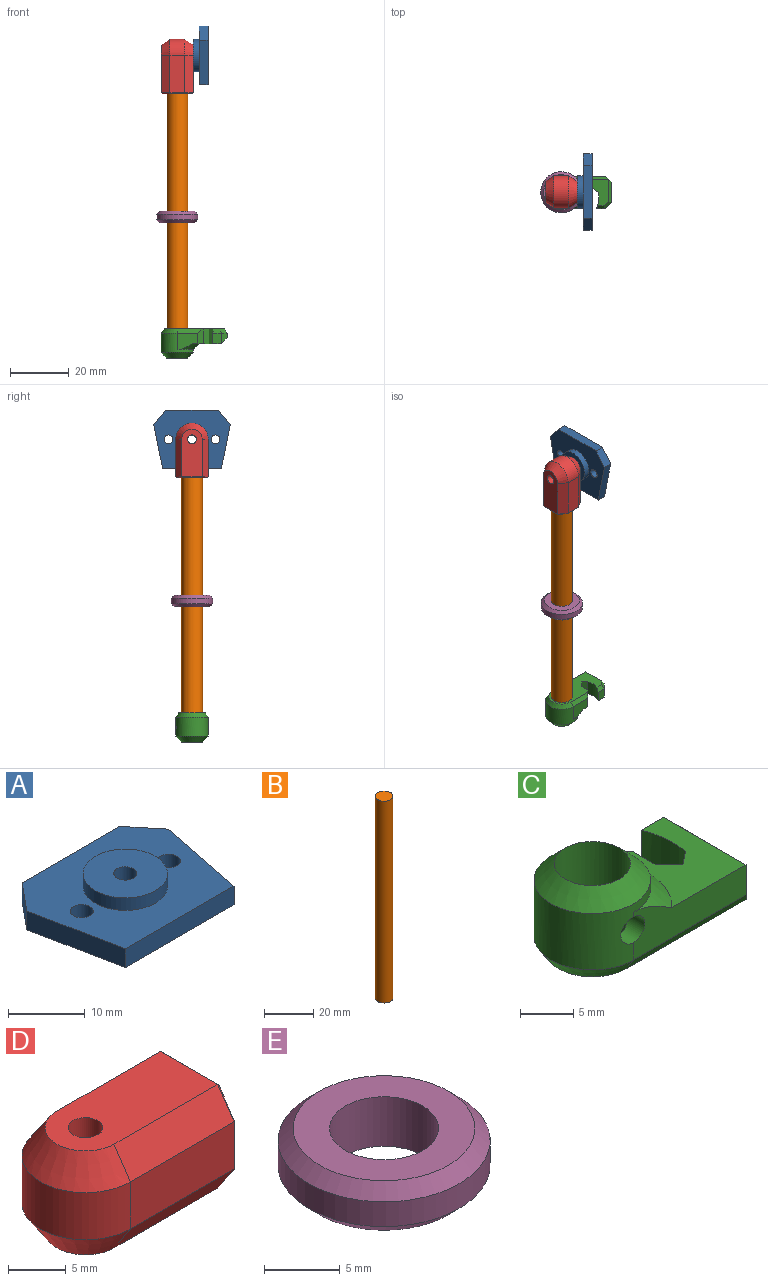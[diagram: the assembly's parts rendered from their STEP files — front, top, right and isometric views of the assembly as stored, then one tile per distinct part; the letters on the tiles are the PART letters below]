
ASSEMBLY  parts=5 mates=4
PART A: 13 faces, bbox 26x20x5 mm
  f0: plane 18x3mm, normal (0,1,0), area 54mm2, adj f7,f8,f9,f10
  f1: plane 15.1x3.02mm, normal (-0.98,-0.2,0), area 46.2mm2, adj f2,f7,f8,f10
  f2: plane 20x3mm, normal (0,-1,0), area 60mm2, adj f1,f3,f7,f8
  f3: plane 15.1x3.02mm, normal (0.98,-0.2,0), area 46.2mm2, adj f2,f7,f8,f9
  f4: cylinder r=1.5mm len=3mm, axis (0,0,1), area 28.3mm2, adj f7,f8
  f5: cylinder r=1.5mm len=3mm, axis (0,0,1), area 28.3mm2, adj f7,f8
  f6: cylinder r=1.5mm len=5mm, axis (0,0,1), area 47.1mm2, adj f7,f12
  f7: plane 26.04x20mm, normal (0,0,-1), area 434.3mm2, adj f0,f1,f2,f3,f4,f5,f6,f9
  f8: plane 26.04x20mm, normal (0,0,1), area 346.3mm2, adj f0,f1,f2,f3,f4,f5,f9,f10
  f9: plane 4.9x4.02mm, normal (0.77,0.63,0), area 19mm2, adj f0,f3,f7,f8
  f10: plane 4.9x4.02mm, normal (-0.77,0.63,0), area 19mm2, adj f0,f1,f7,f8
  f11: cylinder r=5.5mm len=11mm, axis (0,0,-1), area 69.1mm2, adj f8,f12
  f12: plane 11x11mm, normal (0,0,1), area 88mm2, adj f6,f11
PART B: 3 faces, bbox 7.2x7.2x100 mm
  f0: cylinder r=3.6mm len=100mm, axis (0,0,-1), area 2261.9mm2, adj f1,f2
  f1: plane 7.2x7.2mm, normal (0,0,1), area 40.7mm2, adj f0
  f2: plane 7.2x7.2mm, normal (0,0,-1), area 40.7mm2, adj f0
PART C: 25 faces, bbox 22.5x15x9.9 mm
  f0: plane 5x3mm, normal (1,0,0), area 15mm2, adj f8,f9,f10,f12
  f1: plane 7x5.5mm, normal (0,1,0), area 31.1mm2, adj f2,f9,f12,f16,f21
  f2: cylinder r=5.5mm len=11mm, axis (0,0,1), area 126mm2, adj f1,f3,f16,f17,f18,f20
  f3: plane 15x5.5mm, normal (0,-1,0), area 55.6mm2, adj f2,f9,f13,f16,f18,f19
  f4: plane 7x1.5mm, normal (1,0,0), area 10.5mm2, adj f13,f14,f15,f22
  f5: plane 3.5x3mm, normal (0,1,0), area 10.5mm2, adj f6,f9,f15,f24
  f6: cylinder r=9mm len=5.43mm, axis (0,0,1), area 26.9mm2, adj f5,f8,f9,f11,f24
  f7: cylinder r=3.6mm len=9.9mm, axis (0,0,1), area 216.7mm2, adj f8,f17,f18
  f8: plane 20.5x9mm, normal (0,0,-1), area 115.6mm2, adj f0,f6,f7,f10,f11,f12,f19,f20
  f9: plane 11x9.9mm, normal (0,0,1), area 67.5mm2, adj f0,f1,f3,f5,f6,f10,f11,f12
  f10: plane 5x1.8mm, normal (0.71,0.71,0), area 12.7mm2, adj f0,f8,f9,f11
  f11: plane 5x1.7mm, normal (-0.63,0.78,0), area 10.9mm2, adj f6,f8,f9,f10
  f12: plane 5x2mm, normal (0.71,0.71,0), area 13.1mm2, adj f0,f1,f8,f9,f21
  f13: plane 5x2mm, normal (0.71,-0.71,0), area 9.2mm2, adj f3,f4,f14,f19,f22
  f14: plane 11x2mm, normal (0.71,0,0.71), area 25.5mm2, adj f4,f9,f13,f15
  f15: plane 3.5x2mm, normal (0.71,0.71,0), area 7.1mm2, adj f4,f5,f14,f23
  f16: cone r=5.5mm half-angle=45deg, axis (0,0,-1), area 37.9mm2, adj f1,f2,f3,f9
  f17: cone r=3.5mm half-angle=45deg, axis (0,0,-1), area 76.8mm2, adj f2,f7
  f18: cylinder r=1.5mm len=3mm, axis (0,-1,0), area 18.9mm2, adj f2,f3,f7
  f19: plane 16x1.5mm, normal (0,-0.83,-0.55), area 27.9mm2, adj f3,f8,f13,f20
  f20: cone r=5.5mm half-angle=33.7deg, axis (0,0,1), area 28.3mm2, adj f2,f8,f19,f21
  f21: plane 8x1.5mm, normal (0,0.83,-0.55), area 13.5mm2, adj f1,f8,f12,f20
  f22: plane 8x1.5mm, normal (0.83,0,-0.55), area 13.1mm2, adj f4,f8,f13,f23
  f23: plane 2.41x2.41mm, normal (0.59,0.59,-0.55), area 4.4mm2, adj f8,f15,f22,f24
  f24: plane 3.02x1.52mm, normal (0,0.83,-0.55), area 4.7mm2, adj f5,f6,f8,f23
PART D: 29 faces, bbox 18.5x11x11 mm
  f0: cylinder r=5.5mm len=11mm, axis (0,0,-1), area 86.4mm2, adj f1,f4,f15,f18
  f1: plane 12.7x5mm, normal (0,-1,0), area 63.5mm2, adj f0,f14,f17,f23
  f2: plane 10.4x10.4mm, normal (1,0,0), area 52.9mm2, adj f7,f8,f9,f10,f11,f12,f21,f22
  f3: cylinder r=1.5mm len=11mm, axis (0,0,-1), area 103.7mm2, adj f5,f6
  f4: plane 12.7x5mm, normal (0,1,0), area 63.5mm2, adj f0,f16,f19,f26
  f5: plane 16.2x7mm, normal (0,0,1), area 101.1mm2, adj f3,f14,f15,f16,f27
  f6: plane 16.2x7mm, normal (0,0,-1), area 94mm2, adj f3,f17,f18,f19,f20,f22
  f7: plane 10x3.6mm, normal (0,0.87,0.5), area 41.6mm2, adj f2,f8,f12,f13
  f8: plane 10x4.16mm, normal (0,0,1), area 34.5mm2, adj f2,f7,f9,f13,f20
  f9: plane 10x3.6mm, normal (0,-0.87,0.5), area 41.6mm2, adj f2,f8,f10,f13
  f10: plane 10x3.6mm, normal (0,-0.87,-0.5), area 41.6mm2, adj f2,f9,f11,f13
  f11: plane 10x4.16mm, normal (0,0,-1), area 41.6mm2, adj f2,f10,f12,f13
  f12: plane 10x3.6mm, normal (0,0.87,-0.5), area 41.6mm2, adj f2,f7,f11,f13
  f13: plane 8.31x7.2mm, normal (1,0,0), area 44.9mm2, adj f7,f8,f9,f10,f11,f12
  f14: plane 12.7x3mm, normal (0,-0.83,0.55), area 45.8mm2, adj f1,f5,f15,f25
  f15: cone r=3.5mm half-angle=33.7deg, axis (0,0,-1), area 51mm2, adj f0,f5,f14,f16
  f16: plane 12.7x3mm, normal (0,0.83,0.55), area 45.8mm2, adj f4,f5,f15,f28
  f17: plane 12.7x3mm, normal (0,-0.83,-0.55), area 45.8mm2, adj f1,f6,f18,f21
  f18: cone r=5.5mm half-angle=33.7deg, axis (0,0,1), area 51mm2, adj f0,f6,f17,f19
  f19: plane 12.7x3mm, normal (0,0.83,-0.55), area 45.8mm2, adj f4,f6,f18,f24
  f20: cylinder r=1.5mm len=3mm, axis (0,0,1), area 17.9mm2, adj f6,f8
  f21: plane 3.09x2.16mm, normal (0.71,-0.59,-0.39), area 1.5mm2, adj f2,f17,f22,f23
  f22: plane 7x0.3mm, normal (0.71,0,-0.71), area 2.9mm2, adj f2,f6,f21,f24
  f23: plane 5x0.3mm, normal (0.71,-0.71,0), area 2.1mm2, adj f1,f2,f21,f25
  f24: plane 3.09x2.16mm, normal (0.71,0.59,-0.39), area 1.5mm2, adj f2,f19,f22,f26
  f25: plane 3.09x2.16mm, normal (0.71,-0.59,0.39), area 1.5mm2, adj f2,f14,f23,f27
  f26: plane 5x0.3mm, normal (0.71,0.71,0), area 2.1mm2, adj f2,f4,f24,f28
  f27: plane 7x0.3mm, normal (0.71,0,0.71), area 2.9mm2, adj f2,f5,f25,f28
  f28: plane 3.09x2.16mm, normal (0.71,0.59,0.39), area 1.5mm2, adj f2,f16,f26,f27
PART E: 6 faces, bbox 14x14x4 mm
  f0: cylinder r=3.6mm len=7.2mm, axis (0,0,-1), area 90.5mm2, adj f2,f3
  f1: cylinder r=7mm len=14mm, axis (0,0,-1), area 88mm2, adj f4,f5
  f2: plane 12x12mm, normal (0,0,1), area 72.4mm2, adj f0,f4
  f3: plane 12x12mm, normal (0,0,-1), area 72.4mm2, adj f0,f5
  f4: cone r=6mm half-angle=45deg, axis (0,0,-1), area 57.8mm2, adj f1,f2
  f5: cone r=7mm half-angle=45deg, axis (0,0,1), area 57.8mm2, adj f1,f3
PLACE A rot(axis=(0.58,-0.58,-0.58),120deg) t=(7.5,-47.88,134)mm fixed
PLACE B t=(65.3,12.43,-46)mm
PLACE C rot(axis=(1,0,0),180deg) t=(0,-72.88,-41.1)mm
PLACE D rot(axis=(0.71,0,-0.71),180deg) t=(0,-47.88,57)mm
PLACE E at identity
MATE fastened B.f0 <-> D.f13  axis (0,0,1) through (0,-47.88,54)mm
MATE revolute D.f0 <-> A.f6  axis (1,0,0) through (5.5,-47.88,57)mm
MATE fastened B.f0 <-> C.f2  axis (0,0,-1) through (0,-47.88,-46)mm
MATE fastened B.f0 <-> E.f0  axis (0,0,-1) through (0,-47.88,4)mm
